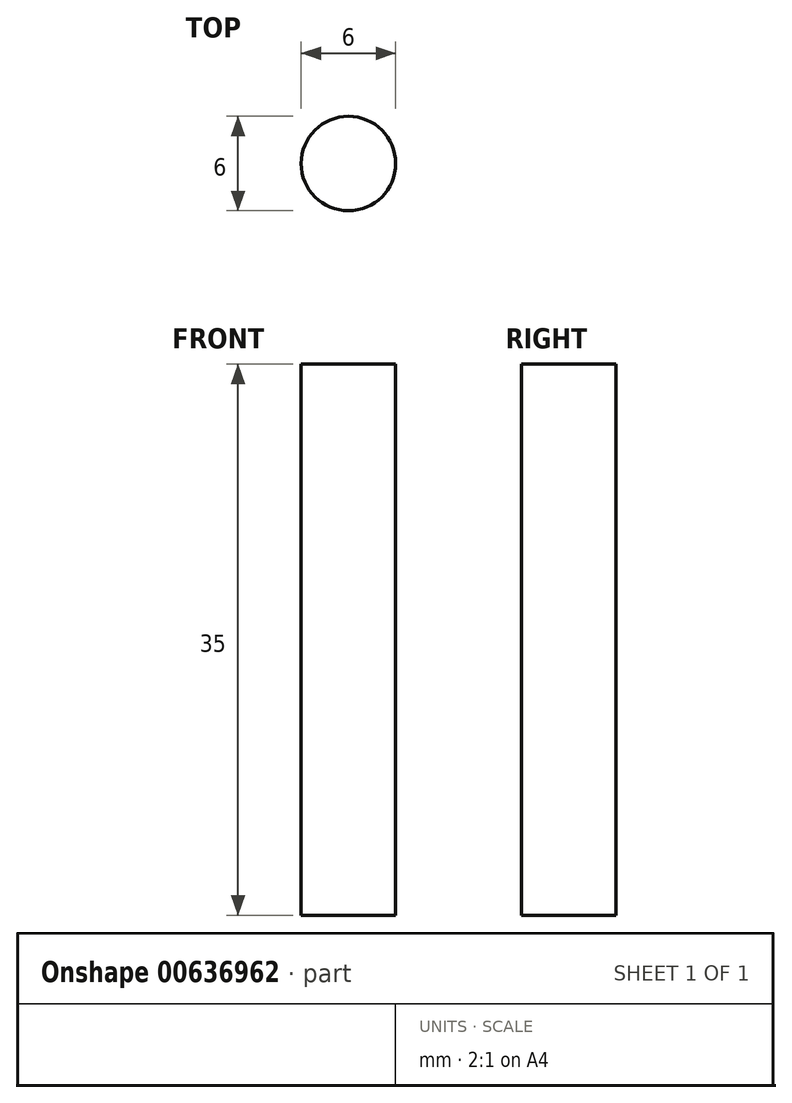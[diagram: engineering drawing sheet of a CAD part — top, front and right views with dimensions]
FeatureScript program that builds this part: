
annotation { "Feature Type Name" : "Feature", "Feature Type Description" : "" }
export const myFeature = defineFeature(function(context is Context, id is Id, definition is map)
    precondition{}
    {
        {
            var Q0;
            Q0=qCreatedBy(makeId("Top.planeOp"),FACE);
            var sketch = newSketch(context, id + "F0", { "sketchPlane" : qUnion([Q0])});
            skCircle(sketch, "E0", {"center": v(0, 0) * mm, "radius": 3 * mm});
            skSolve(sketch);
        }
        {
            var Q0;
            Q0=qSketchRegion(id+"F0",true);
            extrude(context, id + "F1", {"entities" : qUnion([Q0]), "depth" : 35 * mm});
        }
    });
